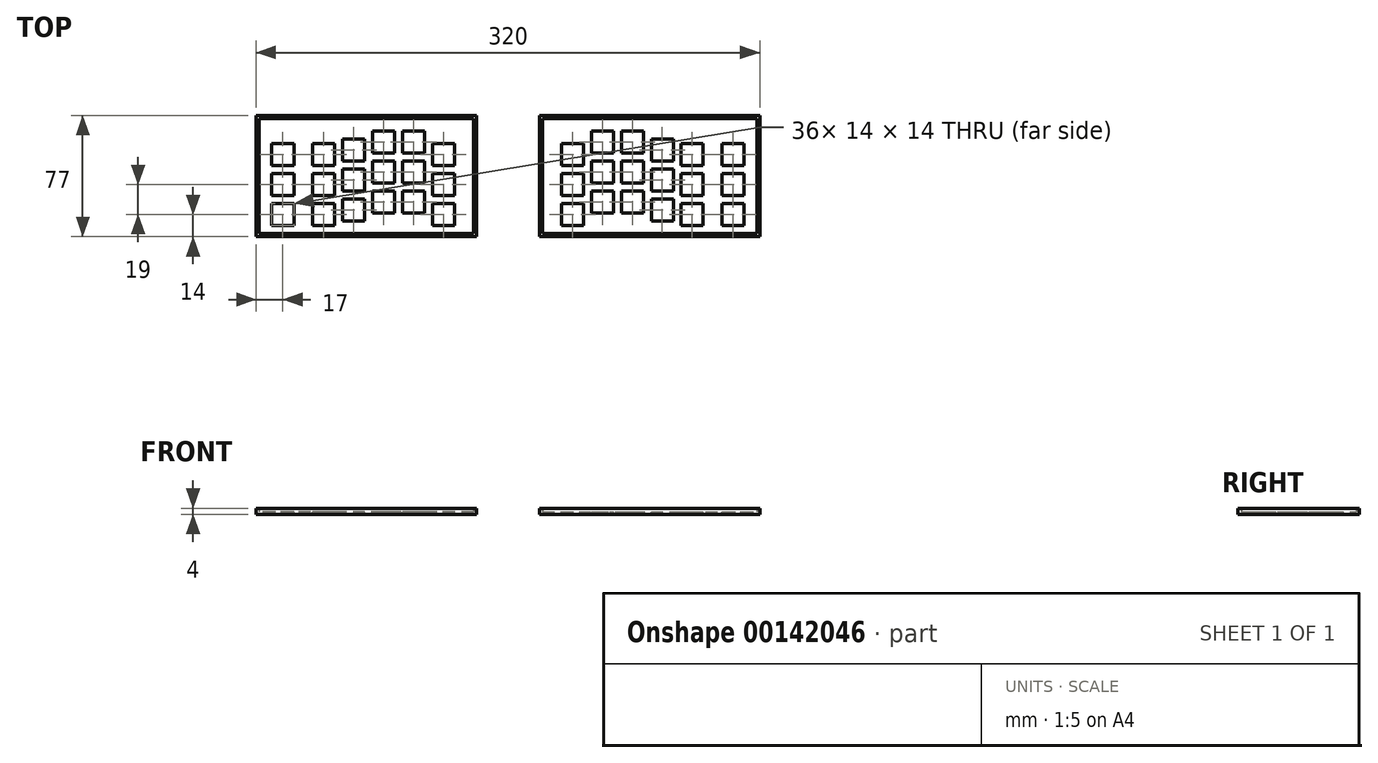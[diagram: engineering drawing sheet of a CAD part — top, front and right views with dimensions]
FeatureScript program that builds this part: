
annotation { "Feature Type Name" : "Feature", "Feature Type Description" : "" }
export const myFeature = defineFeature(function(context is Context, id is Id, definition is map)
    precondition{}
    {
        {
            var Q0;
            Q0=qCreatedBy(makeId("Top.planeOp"),FACE);
            var sketch = newSketch(context, id + "F0", { "sketchPlane" : qUnion([Q0])});
            skLineSegment(sketch, "E0.bottom", {"start": v(70, -38.5) * mm, "end": v(-70, -38.5) * mm});
            skLineSegment(sketch, "E0.top", {"start": v(70, 38.5) * mm, "end": v(-70, 38.5) * mm});
            skLineSegment(sketch, "E0.left", {"start": v(70, -38.5) * mm, "end": v(70, 38.5) * mm});
            skLineSegment(sketch, "E0.right", {"start": v(-70, -38.5) * mm, "end": v(-70, 38.5) * mm});
            skPoint(sketch, "E0.middle", {"position": v(0, 0) * mm});
            skLineSegment(sketch, "E1.bottom", {"start": v(-68, 36.5) * mm, "end": v(68, 36.5) * mm});
            skLineSegment(sketch, "E1.top", {"start": v(-68, -36.5) * mm, "end": v(68, -36.5) * mm});
            skLineSegment(sketch, "E1.left", {"start": v(-68, 36.5) * mm, "end": v(-68, -36.5) * mm});
            skLineSegment(sketch, "E1.right", {"start": v(68, 36.5) * mm, "end": v(68, -36.5) * mm});
            skLineSegment(sketch, "E2", {"start": v(-70, 2.64) * mm, "end": v(-68, 2.64) * mm});
            skLineSegment(sketch, "E3", {"start": v(-20.27, 38.5) * mm, "end": v(-20.27, 36.5) * mm});
            skLineSegment(sketch, "E4", {"start": v(-9.65, -36.5) * mm, "end": v(-9.65, -38.5) * mm});
            skLineSegment(sketch, "E5", {"start": v(68, -5.23) * mm, "end": v(70, -5.23) * mm});
            skSolve(sketch);
        }
        {
            var Q0;
            Q0=makeQuery(id+"F0.imprint","IMPRINT",FACE,{"disambiguationData":[TD([[makeQuery(id+"F0.imprint","IMPRINT",EDGE,{"derivedFrom":sQuery(id+"F0.wireOp",EDGE,"E0.bottom")}),-1.0]])]});
            var Q1;
            {var subQ3=sQuery(id+"F0.wireOp",EDGE,"E2");Q1=makeQuery(id+"F0.imprint","IMPRINT",FACE,{"disambiguationData":[TD([[makeQuery(id+"F0.imprint","IMPRINT",EDGE,{"derivedFrom":subQ3}),1.0]])]});}
            var Q2;
            {var subQ4=sQuery(id+"F0.wireOp",EDGE,"E3");Q2=makeQuery(id+"F0.imprint","IMPRINT",FACE,{"disambiguationData":[TD([[makeQuery(id+"F0.imprint","IMPRINT",EDGE,{"derivedFrom":subQ4}),1.0]])]});}
            var Q3;
            {var subQ4=sQuery(id+"F0.wireOp",EDGE,"E1.left");var subQ6=sQuery(id+"F0.wireOp",EDGE,"E1.bottom");var subQ9=makeQuery(id+"F0.imprint","INTERSECT",VERTEX,{"derivedFrom":[subQ6,subQ4]});Q3=makeQuery(id+"F0.imprint","IMPRINT",FACE,{"disambiguationData":[TD([[makeQuery(id+"F0.imprint","IMPRINT",EDGE,{"disambiguationData":[TD([[subQ9,-1.0]])],"derivedFrom":subQ6}),-1.0]])]});}
            extrude(context, id + "F1", {"entities" : qUnion([Q0, Q1, Q2, Q3]), "depth" : 1.5 * mm});
        }
        {
            var Q0;
            Q0=makeQuery(id+"F1.opExtrude","CAP_FACE",FACE,{"disambiguationData":[OSD([sQuery(id+"F0.wireOp",EDGE,"E0.bottom"),sQuery(id+"F0.wireOp",EDGE,"E0.top"),sQuery(id+"F0.wireOp",EDGE,"E0.left"),sQuery(id+"F0.wireOp",EDGE,"E0.right")])],"isStart":false});
            var sketch = newSketch(context, id + "F2", { "sketchPlane" : qUnion([Q0])});
            skLineSegment(sketch, "E6.bottom", {"start": v(-46, 6.5) * mm, "end": v(-60, 6.5) * mm});
            skLineSegment(sketch, "E6.top", {"start": v(-46, 20.5) * mm, "end": v(-60, 20.5) * mm});
            skLineSegment(sketch, "E6.left", {"start": v(-46, 6.5) * mm, "end": v(-46, 20.5) * mm});
            skLineSegment(sketch, "E6.right", {"start": v(-60, 6.5) * mm, "end": v(-60, 20.5) * mm});
            skPoint(sketch, "E6.middle", {"position": v(-53, 13.5) * mm});
            skLineSegment(sketch, "E7", {"start": v(-53, 20.5) * mm, "end": v(-53, 38.5) * mm});
            skLineSegment(sketch, "E8", {"start": v(-70, 22.6) * mm, "end": v(-60, 22.6) * mm});
            skLineSegment(sketch, "E9.bottom", {"start": v(-46, -12.5) * mm, "end": v(-60, -12.5) * mm});
            skLineSegment(sketch, "E9.top", {"start": v(-46, 1.5) * mm, "end": v(-60, 1.5) * mm});
            skLineSegment(sketch, "E9.left", {"start": v(-46, -12.5) * mm, "end": v(-46, 1.5) * mm});
            skLineSegment(sketch, "E9.right", {"start": v(-60, -12.5) * mm, "end": v(-60, 1.5) * mm});
            skPoint(sketch, "E9.middle", {"position": v(-53, -5.5) * mm});
            skLineSegment(sketch, "E10", {"start": v(-53, 1.5) * mm, "end": v(-53, 6.5) * mm});
            skLineSegment(sketch, "E11", {"start": v(-70, 3.6) * mm, "end": v(-60, 3.6) * mm});
            skLineSegment(sketch, "E12.bottom", {"start": v(-46, -31.5) * mm, "end": v(-60, -31.5) * mm});
            skLineSegment(sketch, "E12.top", {"start": v(-46, -17.5) * mm, "end": v(-60, -17.5) * mm});
            skLineSegment(sketch, "E12.left", {"start": v(-46, -31.5) * mm, "end": v(-46, -17.5) * mm});
            skLineSegment(sketch, "E12.right", {"start": v(-60, -31.5) * mm, "end": v(-60, -17.5) * mm});
            skPoint(sketch, "E12.middle", {"position": v(-53, -24.5) * mm});
            skLineSegment(sketch, "E13", {"start": v(-53, -17.5) * mm, "end": v(-53, -12.5) * mm});
            skLineSegment(sketch, "E14", {"start": v(-70, -15.4) * mm, "end": v(-60, -15.4) * mm});
            skLineSegment(sketch, "E15.bottom", {"start": v(-20, 6.5) * mm, "end": v(-34, 6.5) * mm});
            skLineSegment(sketch, "E15.top", {"start": v(-20, 20.5) * mm, "end": v(-34, 20.5) * mm});
            skLineSegment(sketch, "E15.left", {"start": v(-20, 6.5) * mm, "end": v(-20, 20.5) * mm});
            skLineSegment(sketch, "E15.right", {"start": v(-34, 6.5) * mm, "end": v(-34, 20.5) * mm});
            skPoint(sketch, "E15.middle", {"position": v(-27, 13.5) * mm});
            skLineSegment(sketch, "E16", {"start": v(-27, 20.5) * mm, "end": v(-27, 38.5) * mm});
            skLineSegment(sketch, "E17", {"start": v(-46, 26.44) * mm, "end": v(-34, 26.44) * mm});
            skLineSegment(sketch, "E18.bottom", {"start": v(-20, -12.5) * mm, "end": v(-34, -12.5) * mm});
            skLineSegment(sketch, "E18.top", {"start": v(-20, 1.5) * mm, "end": v(-34, 1.5) * mm});
            skLineSegment(sketch, "E18.left", {"start": v(-20, -12.5) * mm, "end": v(-20, 1.5) * mm});
            skLineSegment(sketch, "E18.right", {"start": v(-34, -12.5) * mm, "end": v(-34, 1.5) * mm});
            skPoint(sketch, "E18.middle", {"position": v(-27, -5.5) * mm});
            skLineSegment(sketch, "E19", {"start": v(-27, 1.5) * mm, "end": v(-27, 6.5) * mm});
            skLineSegment(sketch, "E20", {"start": v(-46, 3.6) * mm, "end": v(-34, 3.6) * mm});
            skLineSegment(sketch, "E21.bottom", {"start": v(-20, -31.5) * mm, "end": v(-34, -31.5) * mm});
            skLineSegment(sketch, "E21.top", {"start": v(-20, -17.5) * mm, "end": v(-34, -17.5) * mm});
            skLineSegment(sketch, "E21.left", {"start": v(-20, -31.5) * mm, "end": v(-20, -17.5) * mm});
            skLineSegment(sketch, "E21.right", {"start": v(-34, -31.5) * mm, "end": v(-34, -17.5) * mm});
            skPoint(sketch, "E21.middle", {"position": v(-27, -24.5) * mm});
            skLineSegment(sketch, "E22", {"start": v(-27, -17.5) * mm, "end": v(-27, -12.5) * mm});
            skLineSegment(sketch, "E23", {"start": v(-46, -15.4) * mm, "end": v(-34, -15.4) * mm});
            skLineSegment(sketch, "E24.bottom", {"start": v(-1, 9.5) * mm, "end": v(-15, 9.5) * mm});
            skLineSegment(sketch, "E24.top", {"start": v(-1, 23.5) * mm, "end": v(-15, 23.5) * mm});
            skLineSegment(sketch, "E24.left", {"start": v(-1, 9.5) * mm, "end": v(-1, 23.5) * mm});
            skLineSegment(sketch, "E24.right", {"start": v(-15, 9.5) * mm, "end": v(-15, 23.5) * mm});
            skPoint(sketch, "E24.middle", {"position": v(-8, 16.5) * mm});
            skLineSegment(sketch, "E25", {"start": v(-8, 23.5) * mm, "end": v(-8, 38.5) * mm});
            skLineSegment(sketch, "E26", {"start": v(-20, 37) * mm, "end": v(-15, 37) * mm});
            skLineSegment(sketch, "E27.bottom", {"start": v(-1, -9.5) * mm, "end": v(-15, -9.5) * mm});
            skLineSegment(sketch, "E27.top", {"start": v(-1, 4.5) * mm, "end": v(-15, 4.5) * mm});
            skLineSegment(sketch, "E27.left", {"start": v(-1, -9.5) * mm, "end": v(-1, 4.5) * mm});
            skLineSegment(sketch, "E27.right", {"start": v(-15, -9.5) * mm, "end": v(-15, 4.5) * mm});
            skPoint(sketch, "E27.middle", {"position": v(-8, -2.5) * mm});
            skLineSegment(sketch, "E28", {"start": v(-8, 4.5) * mm, "end": v(-8, 9.5) * mm});
            skLineSegment(sketch, "E29", {"start": v(-20, 18) * mm, "end": v(-15, 18) * mm});
            skLineSegment(sketch, "E30.bottom", {"start": v(-1, -28.5) * mm, "end": v(-15, -28.5) * mm});
            skLineSegment(sketch, "E30.top", {"start": v(-1, -14.5) * mm, "end": v(-15, -14.5) * mm});
            skLineSegment(sketch, "E30.left", {"start": v(-1, -28.5) * mm, "end": v(-1, -14.5) * mm});
            skLineSegment(sketch, "E30.right", {"start": v(-15, -28.5) * mm, "end": v(-15, -14.5) * mm});
            skPoint(sketch, "E30.middle", {"position": v(-8, -21.5) * mm});
            skLineSegment(sketch, "E31", {"start": v(-8, -14.5) * mm, "end": v(-8, -9.5) * mm});
            skLineSegment(sketch, "E32", {"start": v(-20, -1) * mm, "end": v(-15, -1) * mm});
            skLineSegment(sketch, "E33", {"start": v(-20, -14.9) * mm, "end": v(-15, -14.9) * mm});
            skLineSegment(sketch, "E34.bottom", {"start": v(18, 14.5) * mm, "end": v(4, 14.5) * mm});
            skLineSegment(sketch, "E34.top", {"start": v(18, 28.5) * mm, "end": v(4, 28.5) * mm});
            skLineSegment(sketch, "E34.left", {"start": v(18, 14.5) * mm, "end": v(18, 28.5) * mm});
            skLineSegment(sketch, "E34.right", {"start": v(4, 14.5) * mm, "end": v(4, 28.5) * mm});
            skPoint(sketch, "E34.middle", {"position": v(11, 21.5) * mm});
            skLineSegment(sketch, "E35", {"start": v(11, 28.5) * mm, "end": v(11, 38.5) * mm});
            skLineSegment(sketch, "E36", {"start": v(-1, 52.54) * mm, "end": v(4, 52.54) * mm});
            skLineSegment(sketch, "E37.bottom", {"start": v(18, -4.5) * mm, "end": v(4, -4.5) * mm});
            skLineSegment(sketch, "E37.top", {"start": v(18, 9.5) * mm, "end": v(4, 9.5) * mm});
            skLineSegment(sketch, "E37.left", {"start": v(18, -4.5) * mm, "end": v(18, 9.5) * mm});
            skLineSegment(sketch, "E37.right", {"start": v(4, -4.5) * mm, "end": v(4, 9.5) * mm});
            skPoint(sketch, "E37.middle", {"position": v(11, 2.5) * mm});
            skLineSegment(sketch, "E38", {"start": v(11, 9.5) * mm, "end": v(11, 14.5) * mm});
            skLineSegment(sketch, "E39", {"start": v(-1, 33.54) * mm, "end": v(4, 33.54) * mm});
            skLineSegment(sketch, "E40.bottom", {"start": v(18, -23.5) * mm, "end": v(4, -23.5) * mm});
            skLineSegment(sketch, "E40.top", {"start": v(18, -9.5) * mm, "end": v(4, -9.5) * mm});
            skLineSegment(sketch, "E40.left", {"start": v(18, -23.5) * mm, "end": v(18, -9.5) * mm});
            skLineSegment(sketch, "E40.right", {"start": v(4, -23.5) * mm, "end": v(4, -9.5) * mm});
            skPoint(sketch, "E40.middle", {"position": v(11, -16.5) * mm});
            skLineSegment(sketch, "E41", {"start": v(11, -9.5) * mm, "end": v(11, -4.5) * mm});
            skLineSegment(sketch, "E42", {"start": v(-1, 14.54) * mm, "end": v(4, 14.54) * mm});
            skLineSegment(sketch, "E43", {"start": v(-3, 0.65) * mm, "end": v(2, 0.65) * mm});
            skLineSegment(sketch, "E44.bottom", {"start": v(37, 14.5) * mm, "end": v(23, 14.5) * mm});
            skLineSegment(sketch, "E44.top", {"start": v(37, 28.5) * mm, "end": v(23, 28.5) * mm});
            skLineSegment(sketch, "E44.left", {"start": v(37, 14.5) * mm, "end": v(37, 28.5) * mm});
            skLineSegment(sketch, "E44.right", {"start": v(23, 14.5) * mm, "end": v(23, 28.5) * mm});
            skPoint(sketch, "E44.middle", {"position": v(30, 21.5) * mm});
            skLineSegment(sketch, "E45", {"start": v(30, 28.5) * mm, "end": v(30, 38.5) * mm});
            skLineSegment(sketch, "E46", {"start": v(18, 38.32) * mm, "end": v(23, 38.32) * mm});
            skLineSegment(sketch, "E47.bottom", {"start": v(37, -4.5) * mm, "end": v(23, -4.5) * mm});
            skLineSegment(sketch, "E47.top", {"start": v(37, 9.5) * mm, "end": v(23, 9.5) * mm});
            skLineSegment(sketch, "E47.left", {"start": v(37, -4.5) * mm, "end": v(37, 9.5) * mm});
            skLineSegment(sketch, "E47.right", {"start": v(23, -4.5) * mm, "end": v(23, 9.5) * mm});
            skPoint(sketch, "E47.middle", {"position": v(30, 2.5) * mm});
            skLineSegment(sketch, "E48", {"start": v(30, 9.5) * mm, "end": v(30, 14.5) * mm});
            skLineSegment(sketch, "E49", {"start": v(18, 19.32) * mm, "end": v(23, 19.32) * mm});
            skLineSegment(sketch, "E50.bottom", {"start": v(37, -23.5) * mm, "end": v(23, -23.5) * mm});
            skLineSegment(sketch, "E50.top", {"start": v(37, -9.5) * mm, "end": v(23, -9.5) * mm});
            skLineSegment(sketch, "E50.left", {"start": v(37, -23.5) * mm, "end": v(37, -9.5) * mm});
            skLineSegment(sketch, "E50.right", {"start": v(23, -23.5) * mm, "end": v(23, -9.5) * mm});
            skPoint(sketch, "E50.middle", {"position": v(30, -16.5) * mm});
            skLineSegment(sketch, "E51", {"start": v(30, -9.5) * mm, "end": v(30, -4.5) * mm});
            skLineSegment(sketch, "E52", {"start": v(18, 0.32) * mm, "end": v(23, 0.32) * mm});
            skLineSegment(sketch, "E53", {"start": v(16, -13.57) * mm, "end": v(21, -13.57) * mm});
            skLineSegment(sketch, "E54.bottom", {"start": v(56, 6.5) * mm, "end": v(42, 6.5) * mm});
            skLineSegment(sketch, "E54.top", {"start": v(56, 20.5) * mm, "end": v(42, 20.5) * mm});
            skLineSegment(sketch, "E54.left", {"start": v(56, 6.5) * mm, "end": v(56, 20.5) * mm});
            skLineSegment(sketch, "E54.right", {"start": v(42, 6.5) * mm, "end": v(42, 20.5) * mm});
            skPoint(sketch, "E54.middle", {"position": v(49, 13.5) * mm});
            skLineSegment(sketch, "E55", {"start": v(49, 20.5) * mm, "end": v(49, 38.5) * mm});
            skLineSegment(sketch, "E56", {"start": v(37, 58.17) * mm, "end": v(42, 58.17) * mm});
            skLineSegment(sketch, "E57.bottom", {"start": v(56, -12.5) * mm, "end": v(42, -12.5) * mm});
            skLineSegment(sketch, "E57.top", {"start": v(56, 1.5) * mm, "end": v(42, 1.5) * mm});
            skLineSegment(sketch, "E57.left", {"start": v(56, -12.5) * mm, "end": v(56, 1.5) * mm});
            skLineSegment(sketch, "E57.right", {"start": v(42, -12.5) * mm, "end": v(42, 1.5) * mm});
            skPoint(sketch, "E57.middle", {"position": v(49, -5.5) * mm});
            skLineSegment(sketch, "E58", {"start": v(49, 1.5) * mm, "end": v(49, 6.5) * mm});
            skLineSegment(sketch, "E59", {"start": v(37, 39.17) * mm, "end": v(42, 39.17) * mm});
            skLineSegment(sketch, "E60.bottom", {"start": v(56, -31.5) * mm, "end": v(42, -31.5) * mm});
            skLineSegment(sketch, "E60.top", {"start": v(56, -17.5) * mm, "end": v(42, -17.5) * mm});
            skLineSegment(sketch, "E60.left", {"start": v(56, -31.5) * mm, "end": v(56, -17.5) * mm});
            skLineSegment(sketch, "E60.right", {"start": v(42, -31.5) * mm, "end": v(42, -17.5) * mm});
            skPoint(sketch, "E60.middle", {"position": v(49, -24.5) * mm});
            skLineSegment(sketch, "E61", {"start": v(49, -17.5) * mm, "end": v(49, -12.5) * mm});
            skLineSegment(sketch, "E62", {"start": v(37, 20.17) * mm, "end": v(42, 20.17) * mm});
            skLineSegment(sketch, "E63", {"start": v(35, 6.27) * mm, "end": v(40, 6.27) * mm});
            skSolve(sketch);
        }
        {
            var Q0;
            Q0=makeQuery(id+"F2.imprint","IMPRINT",FACE,{"disambiguationData":[TD([[makeQuery(id+"F2.imprint","IMPRINT",EDGE,{"derivedFrom":sQuery(id+"F2.wireOp",EDGE,"5160ac26-ed04-413d-9b32-f3e1fc32083a.bottom")}),-1.0]])]});
            var Q1;
            Q1=makeQuery(id+"F2.imprint","IMPRINT",FACE,{"disambiguationData":[TD([[makeQuery(id+"F2.imprint","IMPRINT",EDGE,{"derivedFrom":sQuery(id+"F2.wireOp",EDGE,"1a541693-ce7a-49de-9253-2c3cedce4c8c.bottom")}),-1.0]])]});
            var Q2;
            Q2=makeQuery(id+"F2.imprint","IMPRINT",FACE,{"disambiguationData":[TD([[makeQuery(id+"F2.imprint","IMPRINT",EDGE,{"derivedFrom":sQuery(id+"F2.wireOp",EDGE,"822350d8-13fb-4985-b970-823914868b5b.bottom")}),-1.0]])]});
            var Q3;
            {var subQ3=sQuery(id+"F2.wireOp",EDGE,"E60.left");Q3=makeQuery(id+"F2.imprint","IMPRINT",FACE,{"disambiguationData":[TD([[makeQuery(id+"F2.imprint","IMPRINT",EDGE,{"derivedFrom":subQ3}),1.0]])]});}
            var Q4;
            Q4=makeQuery(id+"F2.imprint","IMPRINT",FACE,{"disambiguationData":[TD([[makeQuery(id+"F2.imprint","IMPRINT",EDGE,{"derivedFrom":sQuery(id+"F2.wireOp",EDGE,"2a828c5f-72af-4d73-981a-6c97f8c62778.bottom")}),-1.0]])]});
            var Q5;
            {var subQ5=sQuery(id+"F2.wireOp",EDGE,"788d1230-7a42-43d2-857e-88bdd9539fab.bottom");Q5=makeQuery(id+"F2.imprint","IMPRINT",FACE,{"disambiguationData":[TD([[makeQuery(id+"F2.imprint","IMPRINT",EDGE,{"derivedFrom":subQ5}),-1.0]])]});}
            var Q6;
            {var subQ3=sQuery(id+"F2.wireOp",EDGE,"E24.left");Q6=makeQuery(id+"F2.imprint","IMPRINT",FACE,{"disambiguationData":[TD([[makeQuery(id+"F2.imprint","IMPRINT",EDGE,{"derivedFrom":subQ3}),1.0]])]});}
            var Q7;
            {var subQ0=sQuery(id+"F2.wireOp",EDGE,"E27.right");Q7=makeQuery(id+"F2.imprint","IMPRINT",FACE,{"disambiguationData":[TD([[makeQuery(id+"F2.imprint","IMPRINT",EDGE,{"derivedFrom":subQ0}),-1.0]])]});}
            var Q8;
            {var subQ7=sQuery(id+"F2.wireOp",EDGE,"E30.left");Q8=makeQuery(id+"F2.imprint","IMPRINT",FACE,{"disambiguationData":[TD([[makeQuery(id+"F2.imprint","IMPRINT",EDGE,{"derivedFrom":subQ7}),1.0]])]});}
            var Q9;
            {var subQ4=sQuery(id+"F2.wireOp",EDGE,"E34.left");Q9=makeQuery(id+"F2.imprint","IMPRINT",FACE,{"disambiguationData":[TD([[makeQuery(id+"F2.imprint","IMPRINT",EDGE,{"derivedFrom":subQ4}),1.0]])]});}
            var Q10;
            {var subQ7=sQuery(id+"F2.wireOp",EDGE,"E37.left");Q10=makeQuery(id+"F2.imprint","IMPRINT",FACE,{"disambiguationData":[TD([[makeQuery(id+"F2.imprint","IMPRINT",EDGE,{"derivedFrom":subQ7}),1.0]])]});}
            var Q11;
            {var subQ0=sQuery(id+"F2.wireOp",EDGE,"E40.right");Q11=makeQuery(id+"F2.imprint","IMPRINT",FACE,{"disambiguationData":[TD([[makeQuery(id+"F2.imprint","IMPRINT",EDGE,{"derivedFrom":subQ0}),-1.0]])]});}
            var Q12;
            {var subQ4=sQuery(id+"F2.wireOp",EDGE,"E50.left");Q12=makeQuery(id+"F2.imprint","IMPRINT",FACE,{"disambiguationData":[TD([[makeQuery(id+"F2.imprint","IMPRINT",EDGE,{"derivedFrom":subQ4}),1.0]])]});}
            var Q13;
            {var subQ8=sQuery(id+"F2.wireOp",EDGE,"E57.left");Q13=makeQuery(id+"F2.imprint","IMPRINT",FACE,{"disambiguationData":[TD([[makeQuery(id+"F2.imprint","IMPRINT",EDGE,{"derivedFrom":subQ8}),1.0]])]});}
            var Q14;
            {var subQ1=sQuery(id+"F2.wireOp",EDGE,"52623f21-bd17-4101-b7f8-4e1afcfc3fa1.bottom");Q14=makeQuery(id+"F2.imprint","IMPRINT",FACE,{"disambiguationData":[TD([[makeQuery(id+"F2.imprint","IMPRINT",EDGE,{"derivedFrom":subQ1}),-1.0]])]});}
            var Q15;
            {var subQ4=sQuery(id+"F2.wireOp",EDGE,"E15.left");var subQ11=makeQuery(id+"F2.imprint","IMPRINT",VERTEX,{"derivedFrom":subQ4});Q15=makeQuery(id+"F2.imprint","IMPRINT",FACE,{"disambiguationData":[TD([[makeQuery(id+"F2.imprint","IMPRINT",EDGE,{"disambiguationData":[TD([[subQ11,1.0]])],"derivedFrom":subQ4}),1.0]])]});}
            var Q16;
            {var subQ4=sQuery(id+"F2.wireOp",EDGE,"E18.left");var subQ11=makeQuery(id+"F2.imprint","IMPRINT",VERTEX,{"derivedFrom":subQ4});Q16=makeQuery(id+"F2.imprint","IMPRINT",FACE,{"disambiguationData":[TD([[makeQuery(id+"F2.imprint","IMPRINT",EDGE,{"disambiguationData":[TD([[subQ11,1.0]])],"derivedFrom":subQ4}),1.0]])]});}
            var Q17;
            {var subQ0=sQuery(id+"F2.wireOp",EDGE,"E44.right");var subQ10=makeQuery(id+"F2.imprint","IMPRINT",VERTEX,{"derivedFrom":subQ0});Q17=makeQuery(id+"F2.imprint","IMPRINT",FACE,{"disambiguationData":[TD([[makeQuery(id+"F2.imprint","IMPRINT",EDGE,{"disambiguationData":[TD([[subQ10,1.0]])],"derivedFrom":subQ0}),-1.0]])]});}
            var Q18;
            {var subQ0=sQuery(id+"F2.wireOp",EDGE,"E47.right");var subQ6=makeQuery(id+"F2.imprint","IMPRINT",VERTEX,{"derivedFrom":subQ0});Q18=makeQuery(id+"F2.imprint","IMPRINT",FACE,{"disambiguationData":[TD([[makeQuery(id+"F2.imprint","IMPRINT",EDGE,{"disambiguationData":[TD([[subQ6,1.0]])],"derivedFrom":subQ0}),-1.0]])]});}
            var Q19;
            {var subQ4=sQuery(id+"F2.wireOp",EDGE,"E54.left");Q19=makeQuery(id+"F2.imprint","IMPRINT",FACE,{"disambiguationData":[TD([[makeQuery(id+"F2.imprint","IMPRINT",EDGE,{"derivedFrom":subQ4}),1.0]])]});}
            var Q20;
            {var subQ4=sQuery(id+"F2.wireOp",EDGE,"E6.left");var subQ6=sQuery(id+"F2.wireOp",EDGE,"E6.bottom");var subQ9=makeQuery(id+"F2.imprint","INTERSECT",VERTEX,{"derivedFrom":[subQ6,subQ4]});Q20=makeQuery(id+"F2.imprint","IMPRINT",FACE,{"disambiguationData":[TD([[makeQuery(id+"F2.imprint","IMPRINT",EDGE,{"disambiguationData":[TD([[subQ9,-1.0]])],"derivedFrom":subQ6}),-1.0]])]});}
            var Q21;
            {var subQ4=sQuery(id+"F2.wireOp",EDGE,"E12.bottom");var subQ7=sQuery(id+"F2.wireOp",EDGE,"E12.left");var subQ10=makeQuery(id+"F2.imprint","INTERSECT",VERTEX,{"derivedFrom":[subQ4,subQ7]});Q21=makeQuery(id+"F2.imprint","IMPRINT",FACE,{"disambiguationData":[TD([[makeQuery(id+"F2.imprint","IMPRINT",EDGE,{"disambiguationData":[TD([[subQ10,-1.0]])],"derivedFrom":subQ4}),-1.0]])]});}
            var Q22;
            {var subQ4=sQuery(id+"F2.wireOp",EDGE,"E9.left");var subQ6=sQuery(id+"F2.wireOp",EDGE,"E9.bottom");var subQ9=makeQuery(id+"F2.imprint","INTERSECT",VERTEX,{"derivedFrom":[subQ6,subQ4]});Q22=makeQuery(id+"F2.imprint","IMPRINT",FACE,{"disambiguationData":[TD([[makeQuery(id+"F2.imprint","IMPRINT",EDGE,{"disambiguationData":[TD([[subQ9,-1.0]])],"derivedFrom":subQ6}),-1.0]])]});}
            var Q23;
            {var subQ4=sQuery(id+"F2.wireOp",EDGE,"E21.bottom");var subQ7=sQuery(id+"F2.wireOp",EDGE,"E21.left");var subQ8=makeQuery(id+"F2.imprint","INTERSECT",VERTEX,{"derivedFrom":[subQ4,subQ7]});Q23=makeQuery(id+"F2.imprint","IMPRINT",FACE,{"disambiguationData":[TD([[makeQuery(id+"F2.imprint","IMPRINT",EDGE,{"disambiguationData":[TD([[subQ8,-1.0]])],"derivedFrom":subQ4}),-1.0]])]});}
            var Q24;
            {var subQ0=sQuery(id+"F2.wireOp",EDGE,"E15.right");Q24=makeQuery(id+"F2.imprint","IMPRINT",FACE,{"disambiguationData":[TD([[makeQuery(id+"F2.imprint","IMPRINT",EDGE,{"derivedFrom":subQ0}),-1.0]])]});}
            var Q25;
            {var subQ4=sQuery(id+"F2.wireOp",EDGE,"E18.left");var subQ6=sQuery(id+"F2.wireOp",EDGE,"E18.bottom");var subQ9=makeQuery(id+"F2.imprint","INTERSECT",VERTEX,{"derivedFrom":[subQ6,subQ4]});Q25=makeQuery(id+"F2.imprint","IMPRINT",FACE,{"disambiguationData":[TD([[makeQuery(id+"F2.imprint","IMPRINT",EDGE,{"disambiguationData":[TD([[subQ9,-1.0]])],"derivedFrom":subQ6}),-1.0]])]});}
            var Q26;
            {var subQ8=sQuery(id+"F2.wireOp",EDGE,"E47.left");var subQ11=makeQuery(id+"F2.imprint","IMPRINT",VERTEX,{"derivedFrom":subQ8});Q26=makeQuery(id+"F2.imprint","IMPRINT",FACE,{"disambiguationData":[TD([[makeQuery(id+"F2.imprint","IMPRINT",EDGE,{"disambiguationData":[TD([[subQ11,1.0]])],"derivedFrom":subQ8}),1.0]])]});}
            var Q27;
            {var subQ4=sQuery(id+"F2.wireOp",EDGE,"E44.left");var subQ6=sQuery(id+"F2.wireOp",EDGE,"E44.bottom");var subQ9=makeQuery(id+"F2.imprint","INTERSECT",VERTEX,{"derivedFrom":[subQ6,subQ4]});Q27=makeQuery(id+"F2.imprint","IMPRINT",FACE,{"disambiguationData":[TD([[makeQuery(id+"F2.imprint","IMPRINT",EDGE,{"disambiguationData":[TD([[subQ9,-1.0]])],"derivedFrom":subQ6}),-1.0]])]});}
            var Q28;
            {var subQ4=sQuery(id+"F2.wireOp",EDGE,"E47.left");Q28=makeQuery(id+"F2.imprint","IMPRINT",FACE,{"disambiguationData":[TD([[makeQuery(id+"F2.imprint","IMPRINT",EDGE,{"derivedFrom":subQ4}),1.0]])]});}
            extrude(context, id + "F3", {"entities" : qUnion([Q0, Q1, Q2, Q3, Q4, Q5, Q6, Q7, Q8, Q9, Q10, Q11, Q12, Q13, Q14, Q15, Q16, Q17, Q18, Q19, Q20, Q21, Q22, Q23, Q24, Q25, Q26, Q27, Q28]), "operationType" : NewBodyOperationType.REMOVE, "oppositeDirection" : true, "depth" : 25 * mm});
        }
        {
            var Q0;
            Q0 = qSketchRegion(id + "F0", true);
            extrude(context, id + "F4", {"entities" : qUnion([Q0]), "operationType" : NewBodyOperationType.ADD, "depth" : 4 * mm});
        }
        {
            var Q0;
            Q0=qCreatedBy(makeId("Right.planeOp"),FACE);
            cPlane(context, id + "F5", {"entities" : qUnion([Q0]), "cplaneType" : CPlaneType.OFFSET, "offset" : 90 * mm, "width" : 150 * mm, "height" : 150 * mm});
        }
        {
            var Q0;
            Q0=makeQuery(id+"F1.opExtrude","SWEPT_BODY",BODY,{"disambiguationData":[OSD([sQuery(id+"F0.wireOp",EDGE,"E0.bottom"),sQuery(id+"F0.wireOp",EDGE,"E0.top"),sQuery(id+"F0.wireOp",EDGE,"E0.left"),sQuery(id+"F0.wireOp",EDGE,"E0.right")])]});
            var Q1;
            Q1=qCreatedBy(id+"F5.planeOp",FACE);
            mirror(context, id + "F6", {"entities" : qUnion([Q0]), "mirrorPlane" : qUnion([Q1])});
        }
    });
